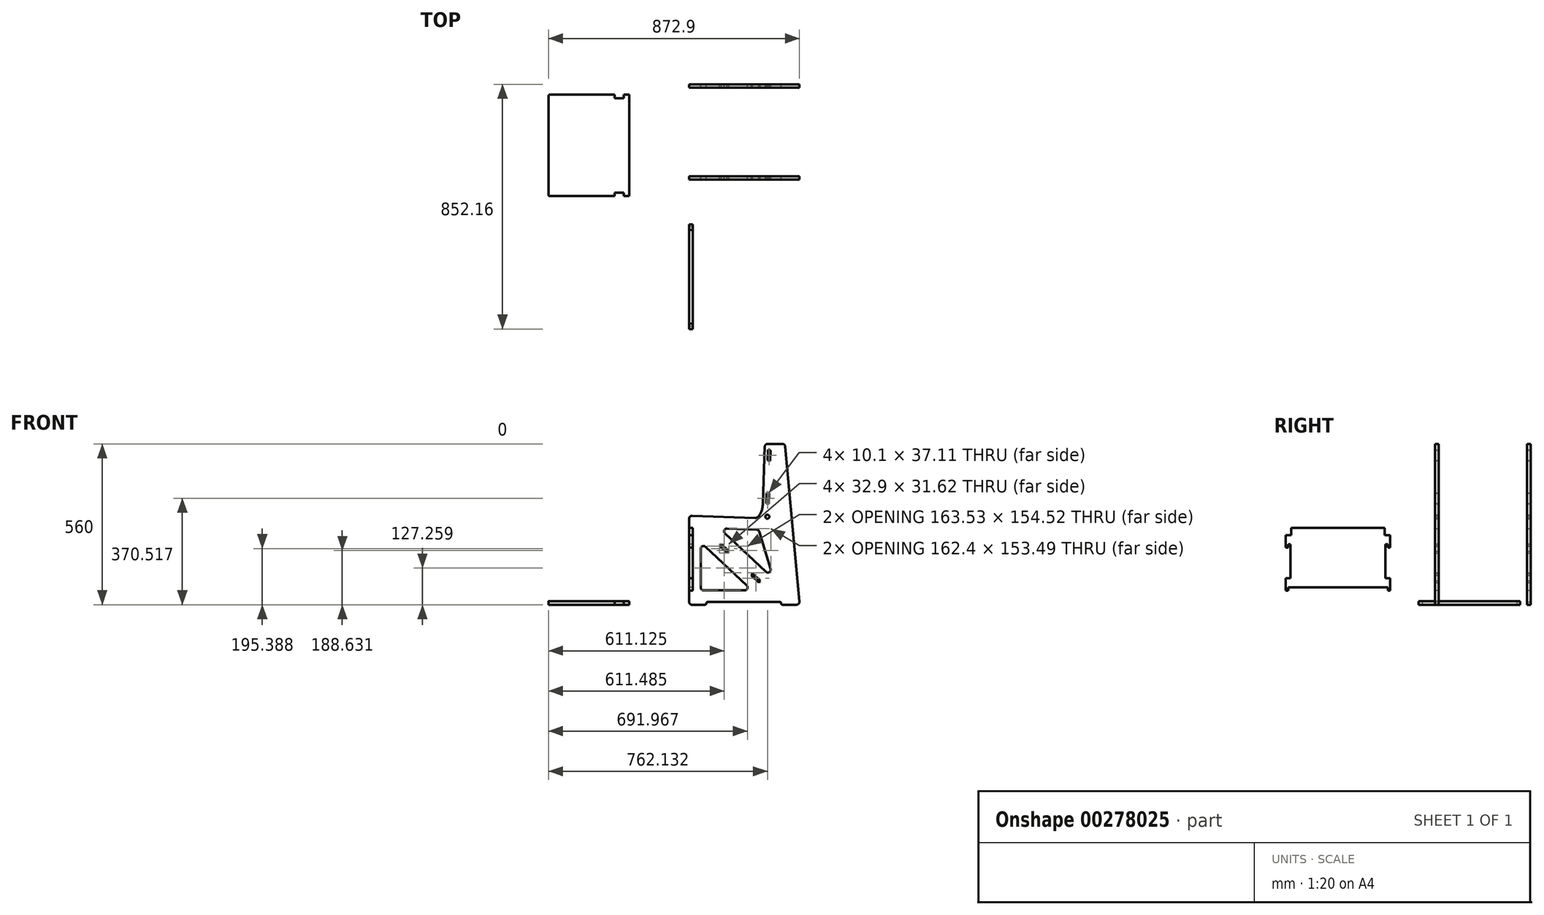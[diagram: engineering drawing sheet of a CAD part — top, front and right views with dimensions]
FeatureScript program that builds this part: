
annotation { "Feature Type Name" : "Feature", "Feature Type Description" : "" }
export const myFeature = defineFeature(function(context is Context, id is Id, definition is map)
    precondition{}
    {
        {
            var Q0;
            Q0=qCreatedBy(makeId("Front.planeOp"),FACE);
            var sketch = newSketch(context, id + "F0", { "sketchPlane" : qUnion([Q0])});
            skLineSegment(sketch, "E0", {"start": v(383.5, 10.9) * mm, "end": v(334.2, 550.9) * mm});
            skLineSegment(sketch, "E1", {"start": v(263.04, 550.35) * mm, "end": v(256.08, 351.09) * mm});
            skLineSegment(sketch, "E2", {"start": v(0, 310) * mm, "end": v(0, 10) * mm});
            skEllipticalArc(sketch, "E3", {});
            skLineSegment(sketch, "E4.0", {"start": v(60, 310) * mm, "end": v(60, 307.9) * mm});
            skLineSegment(sketch, "E5.0", {"start": v(320, 5) * mm, "end": v(320, 5) * mm});
            skLineSegment(sketch, "E6.trimOffspring", {"start": v(60, 5) * mm, "end": v(60, 5) * mm});
            skLineSegment(sketch, "E7.trimOffspring", {"start": v(380, 10) * mm, "end": v(383.58, 10) * mm});
            skPoint(sketch, "E8.visualSharp", {"position": v(333.38, 560) * mm});
            skArc(sketch, "E8.filletArc", {"start": v(334.2, 550.9) * mm, "mid": v(331, 557.39) * mm, "end": v(324.25, 560) * mm});
            skPoint(sketch, "E9.visualSharp", {"position": v(263.38, 560) * mm});
            skArc(sketch, "E9.filletArc", {"start": v(273.04, 560) * mm, "mid": v(266.09, 557.2) * mm, "end": v(263.04, 550.35) * mm});
            skPoint(sketch, "E10.visualSharp", {"position": v(0, 310) * mm});
            skArc(sketch, "E10.filletArc", {"start": v(10.35, 309.64) * mm, "mid": v(3.05, 306.84) * mm, "end": v(0, 299.64) * mm});
            skPoint(sketch, "E11.visualSharp", {"position": v(0, 0) * mm});
            skArc(sketch, "E11.filletArc", {"start": v(0, 10) * mm, "mid": v(2.93, 2.93) * mm, "end": v(10, 0) * mm});
            skPoint(sketch, "E12.visualSharp", {"position": v(384.5, 0) * mm});
            skArc(sketch, "E12.filletArc", {"start": v(373.54, 0) * mm, "mid": v(380.93, 3.26) * mm, "end": v(383.5, 10.9) * mm});
            skPoint(sketch, "E13.visualSharp", {"position": v(60, 10) * mm});
            skArc(sketch, "E13.filletArc", {"start": v(65, 10) * mm, "mid": v(61.46, 8.54) * mm, "end": v(60, 5) * mm});
            skPoint(sketch, "E14.visualSharp", {"position": v(60, 0) * mm});
            skArc(sketch, "E14.filletArc", {"start": v(55, 0) * mm, "mid": v(58.54, 1.46) * mm, "end": v(60, 5) * mm});
            skPoint(sketch, "E15.visualSharp", {"position": v(320, 10) * mm});
            skArc(sketch, "E15.filletArc", {"start": v(320, 5) * mm, "mid": v(318.54, 8.54) * mm, "end": v(315, 10) * mm});
            skPoint(sketch, "E16.visualSharp", {"position": v(320, 0) * mm});
            skArc(sketch, "E16.filletArc", {"start": v(320, 5) * mm, "mid": v(321.46, 1.46) * mm, "end": v(325, 0) * mm});
            skLineSegment(sketch, "E17", {"start": v(243.77, 254.7) * mm, "end": v(283.38, 124.75) * mm});
            skLineSegment(sketch, "E18", {"start": v(0, 310) * mm, "end": v(3.21, 306.99) * mm});
            skLineSegment(sketch, "E19.0", {"start": v(60, 308.58) * mm, "end": v(60.75, 307.88) * mm});
            skLineSegment(sketch, "E20.0", {"start": v(234.55, 261.78) * mm, "end": v(131.71, 265.38) * mm});
            skLineSegment(sketch, "E21.0", {"start": v(50, 50) * mm, "end": v(193.56, 50) * mm});
            skLineSegment(sketch, "E22.trimOffspring", {"start": v(56.84, 201.88) * mm, "end": v(200.4, 67.3) * mm});
            skLineSegment(sketch, "E23.trimOffspring", {"start": v(40, 194.59) * mm, "end": v(40, 60) * mm});
            skLineSegment(sketch, "E24.trimOffspring", {"start": v(124.53, 248.09) * mm, "end": v(266.97, 114.54) * mm});
            skPoint(sketch, "E25.visualSharp", {"position": v(241.69, 261.54) * mm});
            skArc(sketch, "E25.filletArc", {"start": v(243.77, 254.7) * mm, "mid": v(240.3, 259.72) * mm, "end": v(234.55, 261.78) * mm});
            skPoint(sketch, "E26.visualSharp", {"position": v(294.3, 88.92) * mm});
            skArc(sketch, "E26.filletArc", {"start": v(266.97, 114.54) * mm, "mid": v(279.1, 113.35) * mm, "end": v(283.38, 124.75) * mm});
            skPoint(sketch, "E27.visualSharp", {"position": v(105.1, 266.3) * mm});
            skArc(sketch, "E27.filletArc", {"start": v(131.71, 265.38) * mm, "mid": v(122.13, 259.22) * mm, "end": v(124.53, 248.09) * mm});
            skPoint(sketch, "E28.visualSharp", {"position": v(40, 217.67) * mm});
            skArc(sketch, "E28.filletArc", {"start": v(56.84, 201.88) * mm, "mid": v(46.02, 203.76) * mm, "end": v(40, 194.59) * mm});
            skPoint(sketch, "E29.visualSharp", {"position": v(40, 50) * mm});
            skArc(sketch, "E29.filletArc", {"start": v(40, 60) * mm, "mid": v(42.93, 52.93) * mm, "end": v(50, 50) * mm});
            skPoint(sketch, "E30.visualSharp", {"position": v(218.85, 50) * mm});
            skArc(sketch, "E30.filletArc", {"start": v(193.56, 50) * mm, "mid": v(202.86, 56.32) * mm, "end": v(200.4, 67.3) * mm});
            skLineSegment(sketch, "E31", {"start": v(324.25, 560) * mm, "end": v(273.04, 560) * mm});
            skLineSegment(sketch, "E32", {"start": v(373.54, 0) * mm, "end": v(325, 0) * mm});
            skLineSegment(sketch, "E33", {"start": v(65, 10) * mm, "end": v(315, 10) * mm});
            skLineSegment(sketch, "E34", {"start": v(10, 0) * mm, "end": v(55, 0) * mm});
            skLineSegment(sketch, "E35.1", {"start": v(105.67, 204.76) * mm, "end": v(111.71, 211.2) * mm});
            skLineSegment(sketch, "E35.3", {"start": v(132.54, 179.58) * mm, "end": v(138.58, 186.01) * mm});
            skLineSegment(sketch, "E36.0", {"start": v(215.23, 102.3) * mm, "end": v(221.26, 108.74) * mm});
            skLineSegment(sketch, "E36.2", {"start": v(242.1, 77.11) * mm, "end": v(248.13, 83.55) * mm});
            skLineSegment(sketch, "E37.0", {"start": v(274.24, 538.98) * mm, "end": v(283.06, 538.67) * mm});
            skLineSegment(sketch, "E37.1", {"start": v(274.24, 538.98) * mm, "end": v(272.95, 502.18) * mm});
            skLineSegment(sketch, "E37.2", {"start": v(272.95, 502.18) * mm, "end": v(281.77, 501.87) * mm});
            skLineSegment(sketch, "E37.3", {"start": v(283.06, 538.67) * mm, "end": v(281.77, 501.87) * mm});
            skLineSegment(sketch, "E38.0", {"start": v(269, 389.07) * mm, "end": v(277.82, 388.76) * mm});
            skLineSegment(sketch, "E38.1", {"start": v(269, 389.07) * mm, "end": v(267.72, 352.27) * mm});
            skLineSegment(sketch, "E38.2", {"start": v(267.72, 352.27) * mm, "end": v(276.54, 351.96) * mm});
            skLineSegment(sketch, "E38.3", {"start": v(277.82, 388.76) * mm, "end": v(276.54, 351.96) * mm});
            skLineSegment(sketch, "E39.0", {"start": v(221.26, 108.74) * mm, "end": v(248.13, 83.55) * mm});
            skLineSegment(sketch, "E40.0", {"start": v(215.23, 102.3) * mm, "end": v(242.1, 77.11) * mm});
            skLineSegment(sketch, "E41.0", {"start": v(105.67, 204.76) * mm, "end": v(132.54, 179.58) * mm});
            skLineSegment(sketch, "E42.0", {"start": v(111.71, 211.2) * mm, "end": v(138.58, 186.01) * mm});
            skLineSegment(sketch, "E43.0", {"start": v(274.3, 540.57) * mm, "end": v(283.11, 540.26) * mm});
            skLineSegment(sketch, "E44.0", {"start": v(272.9, 500.6) * mm, "end": v(281.72, 500.28) * mm});
            skLineSegment(sketch, "E45.0", {"start": v(269.06, 390.66) * mm, "end": v(277.88, 390.35) * mm});
            skLineSegment(sketch, "E46.0", {"start": v(267.66, 350.68) * mm, "end": v(276.48, 350.38) * mm});
            skCircle(sketch, "E47.0", {"center": v(272.04, 306.5) * mm, "radius": 6.9 * mm});
            skLineSegment(sketch, "E48.trimOffspring", {"start": v(229.35, 302) * mm, "end": v(10.35, 309.64) * mm});
            skLineSegment(sketch, "E49.0", {"start": v(229.56, 307.99) * mm, "end": v(10.56, 315.63) * mm});
            const initialGuessF0  = {"E3": [0.23109916320760213, 0.35196031660683047, 0.9993908270190953, -0.034899496702513765, 0.025, 0.05, 4.71238898038469, 6.283185307179586]};
            skSetInitialGuess(sketch, initialGuessF0);
            skSolve(sketch);
        }
        {
            var Q0;
            {var subQ7=sQuery(id+"F0.wireOp",EDGE,"E0");Q0=makeQuery(id+"F0.imprint","IMPRINT",FACE,{"disambiguationData":[TD([[makeQuery(id+"F0.imprint","IMPRINT",EDGE,{"derivedFrom":subQ7}),1.0]])]});}
            extrude(context, id + "F1", {"entities" : qUnion([Q0]), "depth" : 12 * mm, "offsetDistance" : 25 * mm});
        }
        {
            var Q0;
            Q0=makeQuery(id+"F1.opExtrude","SWEPT_BODY",BODY,{"disambiguationData":[OSD([sQuery(id+"F0.wireOp",EDGE,"lSsndLbL-UpTF-3SSk-Kapd-sRLNuuJKVzhh"),sQuery(id+"F0.wireOp",EDGE,"E0"),sQuery(id+"F0.wireOp",EDGE,"fkqGSsNh-8zb3-kERk-volt-F1pb2TynHZUi"),sQuery(id+"F0.wireOp",EDGE,"E1"),sQuery(id+"F0.wireOp",EDGE,"VmoDCqWj-O8PB-Jrpp-7GfT-6Z7duDKZh1zq"),sQuery(id+"F0.wireOp",EDGE,"E2"),sQuery(id+"F0.wireOp",EDGE,"E3"),sQuery(id+"F0.wireOp",EDGE,"de854aec-d629-46f9-a14c-4f2f3749a6a2.0"),sQuery(id+"F0.wireOp",EDGE,"2167e911-088d-45a9-95b3-6965f1cda39c.trimOffspring"),sQuery(id+"F0.wireOp",EDGE,"E8.filletArc"),sQuery(id+"F0.wireOp",EDGE,"E9.filletArc"),sQuery(id+"F0.wireOp",EDGE,"E10.filletArc"),sQuery(id+"F0.wireOp",EDGE,"E11.filletArc"),sQuery(id+"F0.wireOp",EDGE,"E12.filletArc"),sQuery(id+"F0.wireOp",EDGE,"E13.filletArc"),sQuery(id+"F0.wireOp",EDGE,"E14.filletArc"),sQuery(id+"F0.wireOp",EDGE,"E15.filletArc"),sQuery(id+"F0.wireOp",EDGE,"E16.filletArc"),sQuery(id+"F0.wireOp",EDGE,"E17"),sQuery(id+"F0.wireOp",EDGE,"E20.0"),sQuery(id+"F0.wireOp",EDGE,"E21.0"),sQuery(id+"F0.wireOp",EDGE,"E22.trimOffspring"),sQuery(id+"F0.wireOp",EDGE,"E23.trimOffspring"),sQuery(id+"F0.wireOp",EDGE,"E24.trimOffspring"),sQuery(id+"F0.wireOp",EDGE,"2aa860ef-9c8e-4df4-b0d4-f52292d0f61c.0"),sQuery(id+"F0.wireOp",EDGE,"b5291852-beac-4504-b440-424de1e9b879.0"),sQuery(id+"F0.wireOp",EDGE,"YIcSRTaA-BjjY-Pffc-MHsF-gPfAQwwZ1n3g"),sQuery(id+"F0.wireOp",EDGE,"6bc2c88d-6526-4c92-b775-f08ac1518513.0"),sQuery(id+"F0.wireOp",EDGE,"a2262971-b560-40cb-82d8-bb947d114ada.0"),sQuery(id+"F0.wireOp",EDGE,"a3b99000-b895-41d5-ae90-215d85ffd13a.0"),sQuery(id+"F0.wireOp",EDGE,"d2bb24a6-5df7-4de0-8674-79b6e5bf7214.trimOffspring"),sQuery(id+"F0.wireOp",EDGE,"9221d260-5245-45c5-b231-df6e3a735177.trimOffspring"),sQuery(id+"F0.wireOp",EDGE,"E25.filletArc"),sQuery(id+"F0.wireOp",EDGE,"E26.filletArc"),sQuery(id+"F0.wireOp",EDGE,"E27.filletArc"),sQuery(id+"F0.wireOp",EDGE,"E28.filletArc"),sQuery(id+"F0.wireOp",EDGE,"E29.filletArc"),sQuery(id+"F0.wireOp",EDGE,"E30.filletArc"),sQuery(id+"F0.wireOp",EDGE,"7b93510a-8a0d-4be8-bf8f-d3a81f09d679.0"),sQuery(id+"F0.wireOp",EDGE,"288c4643-272c-46e3-8d73-e5343386492f.0"),sQuery(id+"F0.wireOp",EDGE,"a52265a1-679a-455d-b11c-1bebfbda3813.0"),sQuery(id+"F0.wireOp",EDGE,"1d37ab1c-e848-4acb-9b24-9014ef855f84.0"),sQuery(id+"F0.wireOp",EDGE,"dZBoZdBp-skVY-9oai-LNrl-5jlRIifMk2EM"),sQuery(id+"F0.wireOp",EDGE,"26e25128-ac8b-45fc-a1f7-1c7b8213c6a6.0"),sQuery(id+"F0.wireOp",EDGE,"38e719a8-5ec9-4589-9d27-f48d93014205.trimOffspring"),sQuery(id+"F0.wireOp",EDGE,"465e5268-f64f-496b-8ea4-d922cbf961dc.trimOffspring")])]});
            transform(context, id + "F2", {"entities" : qUnion([Q0]), "transformType" : TransformType.TRANSLATION_3D, "dx" : 0 * mm, "dy" : 320 * mm, "dz" : 0 * mm, "makeCopy" : true});
        }
        {
            var Q0;
            Q0=qCreatedBy(makeId("Top.planeOp"),FACE);
            var sketch = newSketch(context, id + "F3", { "sketchPlane" : qUnion([Q0])});
            skLineSegment(sketch, "E50.right", {"start": v(-489.36, 278.77) * mm, "end": v(-489.36, -64.4) * mm});
            skLineSegment(sketch, "E51.0", {"start": v(-259.36, 283.77) * mm, "end": v(-259.36, 271.77) * mm});
            skLineSegment(sketch, "E52.0", {"start": v(-228.01, 271.77) * mm, "end": v(-259.36, 271.77) * mm});
            skLineSegment(sketch, "E53.0", {"start": v(-228.01, -57.4) * mm, "end": v(-259.36, -57.4) * mm});
            skLineSegment(sketch, "E54.trimOffspring", {"start": v(-259.36, -57.4) * mm, "end": v(-259.36, -69.4) * mm});
            skPoint(sketch, "E55.visualSharp", {"position": v(-489.36, -63.82) * mm});
            skPoint(sketch, "E56.visualSharp", {"position": v(-259.36, -57.4) * mm});
            skLineSegment(sketch, "E57.trimOffspring", {"start": v(-259.36, 283.77) * mm, "end": v(-484.36, 283.77) * mm});
            skArc(sketch, "E58.filletArc", {"start": v(-484.36, 283.77) * mm, "mid": v(-487.9, 282.3) * mm, "end": v(-489.36, 278.77) * mm});
            skLineSegment(sketch, "E59", {"start": v(-259.36, -69.4) * mm, "end": v(-484.36, -69.4) * mm});
            skPoint(sketch, "E60.visualSharp", {"position": v(-489.36, -69.4) * mm});
            skArc(sketch, "E60.filletArc", {"start": v(-489.36, -64.4) * mm, "mid": v(-487.9, -67.94) * mm, "end": v(-484.36, -69.4) * mm});
            skPoint(sketch, "E61.visualSharp", {"position": v(-259.36, -69.4) * mm});
            skLineSegment(sketch, "E62.0", {"start": v(-228.01, 283.77) * mm, "end": v(-228.01, 271.77) * mm});
            skLineSegment(sketch, "E63.0", {"start": v(-208.89, 283.77) * mm, "end": v(-208.89, -69.4) * mm});
            skLineSegment(sketch, "E64", {"start": v(-228.01, 283.77) * mm, "end": v(-208.89, 283.77) * mm});
            skLineSegment(sketch, "E65", {"start": v(-208.89, -69.4) * mm, "end": v(-228.01, -69.4) * mm});
            skLineSegment(sketch, "E66.trimOffspring", {"start": v(-228.01, -57.4) * mm, "end": v(-228.01, -69.4) * mm});
            skSolve(sketch);
        }
        {
            var Q0;
            Q0=qCreatedBy(makeId("Right.planeOp"),FACE);
            var sketch = newSketch(context, id + "F4", { "sketchPlane" : qUnion([Q0])});
            skLineSegment(sketch, "E67", {"start": v(-514.75, 210.83) * mm, "end": v(-523.57, 210.83) * mm});
            skLineSegment(sketch, "E68", {"start": v(-523.57, 198.83) * mm, "end": v(-532.16, 198.83) * mm});
            skLineSegment(sketch, "E69", {"start": v(-532.16, 242) * mm, "end": v(-513.16, 242) * mm});
            skLineSegment(sketch, "E70.0", {"start": v(-532.16, 48.83) * mm, "end": v(-532.16, 92) * mm});
            skLineSegment(sketch, "E71.trimOffspring", {"start": v(-532.16, 198.83) * mm, "end": v(-532.16, 242) * mm});
            skLineSegment(sketch, "E72.0", {"start": v(-532.16, 92) * mm, "end": v(-514.75, 92) * mm});
            skLineSegment(sketch, "E73", {"start": v(-532.16, 48.83) * mm, "end": v(-523.57, 48.83) * mm});
            skLineSegment(sketch, "E74", {"start": v(-513.16, 242) * mm, "end": v(-513.16, 267.83) * mm});
            skLineSegment(sketch, "E75.0", {"start": v(-514.75, 92) * mm, "end": v(-514.75, 210.83) * mm});
            skLineSegment(sketch, "E76.0", {"start": v(-523.57, 198.83) * mm, "end": v(-523.57, 210.83) * mm});
            skLineSegment(sketch, "E77.0", {"start": v(-523.57, 60.83) * mm, "end": v(-523.57, 48.83) * mm});
            skLineSegment(sketch, "E78.MirrorCS", {"start": v(-176.75, 198.83) * mm, "end": v(-168.16, 198.83) * mm});
            skLineSegment(sketch, "E79.MirrorCS", {"start": v(-187.16, 242) * mm, "end": v(-187.16, 267.83) * mm});
            skLineSegment(sketch, "E80.MirrorCS", {"start": v(-185.57, 210.83) * mm, "end": v(-176.75, 210.83) * mm});
            skLineSegment(sketch, "E81.MirrorCS", {"start": v(-176.75, 60.83) * mm, "end": v(-176.75, 48.83) * mm});
            skLineSegment(sketch, "E82.MirrorCS", {"start": v(-176.75, 198.83) * mm, "end": v(-176.75, 210.83) * mm});
            skLineSegment(sketch, "E83.MirrorCS", {"start": v(-168.16, 48.83) * mm, "end": v(-176.75, 48.83) * mm});
            skLineSegment(sketch, "E84.MirrorCS", {"start": v(-168.16, 48.83) * mm, "end": v(-168.16, 92) * mm});
            skLineSegment(sketch, "E85.MirrorCS", {"start": v(-168.16, 92) * mm, "end": v(-185.57, 92) * mm});
            skLineSegment(sketch, "E86.MirrorCS", {"start": v(-185.57, 92) * mm, "end": v(-185.57, 210.83) * mm});
            skLineSegment(sketch, "E87.MirrorCS", {"start": v(-168.16, 242) * mm, "end": v(-187.16, 242) * mm});
            skLineSegment(sketch, "E88.MirrorCS", {"start": v(-168.16, 198.83) * mm, "end": v(-168.16, 242) * mm});
            skLineSegment(sketch, "E89", {"start": v(-187.16, 267.83) * mm, "end": v(-513.16, 267.83) * mm});
            skLineSegment(sketch, "E90", {"start": v(-176.75, 60.83) * mm, "end": v(-523.57, 60.83) * mm});
            skSolve(sketch);
        }
        {
            var Q0;
            Q0=makeQuery(id+"F3.imprint","IMPRINT",FACE,{"disambiguationData":[TD([[makeQuery(id+"F3.imprint","IMPRINT",EDGE,{"derivedFrom":sQuery(id+"F3.wireOp",EDGE,"E50.right")}),1.0]])]});
            extrude(context, id + "F5", {"entities" : qUnion([Q0]), "depth" : 12 * mm, "offsetDistance" : 25 * mm});
        }
        {
            var Q0;
            Q0=makeQuery(id+"F4.imprint","IMPRINT",FACE,{"disambiguationData":[TD([[makeQuery(id+"F4.imprint","IMPRINT",EDGE,{"derivedFrom":sQuery(id+"F4.wireOp",EDGE,"E67")}),-1.0]])]});
            extrude(context, id + "F6", {"entities" : qUnion([Q0]), "depth" : 12 * mm, "offsetDistance" : 25 * mm});
        }
    });
